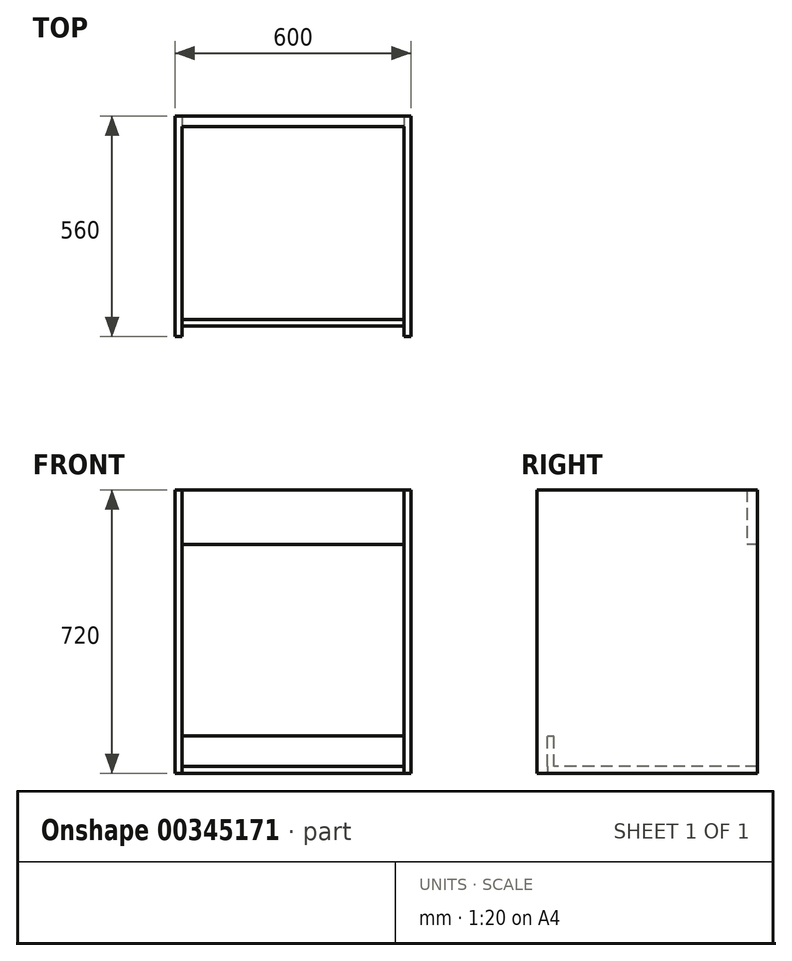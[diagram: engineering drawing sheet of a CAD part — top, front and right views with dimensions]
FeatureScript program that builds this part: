
annotation { "Feature Type Name" : "Feature", "Feature Type Description" : "" }
export const myFeature = defineFeature(function(context is Context, id is Id, definition is map)
    precondition{}
    {
        {
            var Q0;
            Q0=qCreatedBy(makeId("Front.planeOp"),FACE);
            var sketch = newSketch(context, id + "F0", { "sketchPlane" : qUnion([Q0])});
            skLineSegment(sketch, "E0.bottom", {"start": v(0, 0) * mm, "end": v(-52.5, 0) * mm});
            skLineSegment(sketch, "E0.top", {"start": v(0, 40.33) * mm, "end": v(-52.5, 40.33) * mm});
            skLineSegment(sketch, "E0.left", {"start": v(0, 0) * mm, "end": v(0, 40.33) * mm});
            skLineSegment(sketch, "E0.right", {"start": v(-52.5, 0) * mm, "end": v(-52.5, 40.33) * mm});
            skSolve(sketch);
        }
        {
            var Q0;
            Q0=makeQuery(id+"F0.imprint","IMPRINT",FACE,{"disambiguationData":[TD([[makeQuery(id+"F0.imprint","IMPRINT",EDGE,{"derivedFrom":sQuery(id+"F0.wireOp",EDGE,"E0.bottom")}),-1.0]])]});
            extrude(context, id + "F1", {"entities" : qUnion([Q0]), "oppositeDirection" : true, "depth" : 560 * mm});
        }
        {
            var Q0;
            Q0=makeQuery(id+"F1.opExtrude","SWEPT_FACE",FACE,{"disambiguationData":[OSD([sQuery(id+"F0.wireOp",EDGE,"E0.left")])]});
            extrude(context, id + "F2", {"entities" : qUnion([Q0]), "operationType" : NewBodyOperationType.ADD, "oppositeDirection" : true, "depth" : 600 * mm});
        }
        {
            var Q0;
            {var subQ0=sQuery(id+"F0.wireOp",EDGE,"E0.bottom");Q0=makeQuery(id+"F2.boolean.opBoolean","MERGE",FACE,{"derivedFrom":[makeQuery(id+"F1.opExtrude","SWEPT_FACE",FACE,{"disambiguationData":[OSD([subQ0])]}),makeQuery(id+"F2.opExtrude","SWEPT_FACE",FACE,{"disambiguationData":[OSD([subQ0,sQuery(id+"F0.wireOp",EDGE,"E0.left")])]})]});}
            extrude(context, id + "F3", {"entities" : qUnion([Q0]), "operationType" : NewBodyOperationType.ADD, "oppositeDirection" : true, "depth" : 720 * mm});
        }
        {
            var Q0;
            {var subQ0=sQuery(id+"F0.wireOp",EDGE,"E0.left");var subQ1=sQuery(id+"F0.wireOp",EDGE,"E0.bottom");Q0=makeQuery(id+"F3.boolean.opBoolean","MERGE",FACE,{"derivedFrom":[makeQuery(id+"F2.boolean.opBoolean","MERGE",FACE,{"derivedFrom":[makeQuery(id+"F1.opExtrude","CAP_FACE",FACE,{"disambiguationData":[OSD([subQ1,sQuery(id+"F0.wireOp",EDGE,"E0.top"),subQ0,sQuery(id+"F0.wireOp",EDGE,"E0.right")])],"isStart":false}),makeQuery(id+"F2.opExtrude","SWEPT_FACE",FACE,{"disambiguationData":[OSD([subQ0]),TDD([makeQuery(id+"F1.opExtrude","CAP_EDGE",EDGE,{"disambiguationData":[OSD([subQ0])],"isStart":false})])]})]}),makeQuery(id+"F3.opExtrude","SWEPT_FACE",FACE,{"disambiguationData":[OSD([subQ1,subQ0]),TDD([makeQuery(id+"F2.boolean.opBoolean","MERGE",EDGE,{"derivedFrom":[makeQuery(id+"F1.opExtrude","CAP_EDGE",EDGE,{"disambiguationData":[OSD([subQ1])],"isStart":false}),makeQuery(id+"F2.opExtrude","SWEPT_EDGE",EDGE,{"disambiguationData":[OSD([subQ1,subQ0]),TDD([makeQuery(id+"F1.opExtrude","CAP_VERTEX",VERTEX,{"disambiguationData":[OSD([subQ1,subQ0])],"isStart":false})])]})]})])]})]});}
            var Q1;
            Q1=makeQuery(id+"F3.opExtrude","CAP_FACE",FACE,{"disambiguationData":[OSD([sQuery(id+"F0.wireOp",EDGE,"E0.bottom"),sQuery(id+"F0.wireOp",EDGE,"E0.left")])],"isStart":false});
            var Q2;
            {var subQ0=sQuery(id+"F0.wireOp",EDGE,"E0.left");var subQ1=sQuery(id+"F0.wireOp",EDGE,"E0.bottom");Q2=makeQuery(id+"F3.boolean.opBoolean","MERGE",FACE,{"derivedFrom":[makeQuery(id+"F2.boolean.opBoolean","MERGE",FACE,{"derivedFrom":[makeQuery(id+"F1.opExtrude","CAP_FACE",FACE,{"disambiguationData":[OSD([subQ1,sQuery(id+"F0.wireOp",EDGE,"E0.top"),subQ0,sQuery(id+"F0.wireOp",EDGE,"E0.right")])],"isStart":true}),makeQuery(id+"F2.opExtrude","SWEPT_FACE",FACE,{"disambiguationData":[OSD([subQ0]),TDD([makeQuery(id+"F1.opExtrude","CAP_EDGE",EDGE,{"disambiguationData":[OSD([subQ0])],"isStart":true})])]})]}),makeQuery(id+"F3.opExtrude","SWEPT_FACE",FACE,{"disambiguationData":[OSD([subQ1,subQ0]),TDD([makeQuery(id+"F2.boolean.opBoolean","MERGE",EDGE,{"derivedFrom":[makeQuery(id+"F1.opExtrude","CAP_EDGE",EDGE,{"disambiguationData":[OSD([subQ1])],"isStart":true}),makeQuery(id+"F2.opExtrude","SWEPT_EDGE",EDGE,{"disambiguationData":[OSD([subQ1,subQ0]),TDD([makeQuery(id+"F1.opExtrude","CAP_VERTEX",VERTEX,{"disambiguationData":[OSD([subQ1,subQ0])],"isStart":true})])]})]})])]})]});}
            shell(context, id + "F4", {"entities" : qUnion([Q0, Q1, Q2]), "thickness" : 18 * mm});
        }
        {
            var Q0;
            {var subQ0=sQuery(id+"F0.wireOp",EDGE,"E0.left");var subQ1=sQuery(id+"F0.wireOp",EDGE,"E0.bottom");Q0=makeQuery(id+"F4.opShell","OFFSET_FACE",FACE,{"disambiguationData":[OSD([subQ1,subQ0]),TDD([makeQuery(id+"F3.boolean.opBoolean","MERGE",FACE,{"derivedFrom":[makeQuery(id+"F1.opExtrude","SWEPT_FACE",FACE,{"disambiguationData":[OSD([subQ0])]}),makeQuery(id+"F3.opExtrude","SWEPT_FACE",FACE,{"disambiguationData":[OSD([subQ1,subQ0]),TDD([makeQuery(id+"F1.opExtrude","SWEPT_EDGE",EDGE,{"disambiguationData":[OSD([subQ1,subQ0])]})])]})]})])]});}
            var sketch = newSketch(context, id + "F5", { "sketchPlane" : qUnion([Q0])});
            skLineSegment(sketch, "E1.bottom", {"start": v(-560, 720) * mm, "end": v(-532.8, 720) * mm});
            skLineSegment(sketch, "E1.top", {"start": v(-560, 581.74) * mm, "end": v(-532.8, 581.74) * mm});
            skLineSegment(sketch, "E1.left", {"start": v(-560, 720) * mm, "end": v(-560, 581.74) * mm});
            skLineSegment(sketch, "E1.right", {"start": v(-532.8, 720) * mm, "end": v(-532.8, 581.74) * mm});
            skSolve(sketch);
        }
        {
            var Q0;
            Q0=makeQuery(id+"F5.imprint","IMPRINT",FACE,{"disambiguationData":[TD([[makeQuery(id+"F5.imprint","IMPRINT",EDGE,{"derivedFrom":sQuery(id+"F5.wireOp",EDGE,"E1.bottom")}),-1.0]])]});
            extrude(context, id + "F6", {"entities" : qUnion([Q0]), "operationType" : NewBodyOperationType.ADD, "depth" : 562 * mm});
        }
        {
            var Q0;
            Q0=makeQuery(id+"F6.opExtrude","CAP_FACE",FACE,{"disambiguationData":[OSD([sQuery(id+"F5.wireOp",EDGE,"E1.bottom"),sQuery(id+"F5.wireOp",EDGE,"E1.top"),sQuery(id+"F5.wireOp",EDGE,"E1.left"),sQuery(id+"F5.wireOp",EDGE,"E1.right")])],"isStart":false});
            extrude(context, id + "F7", {"entities" : qUnion([Q0]), "operationType" : NewBodyOperationType.ADD, "depth" : 2 * mm});
        }
        {
            var Q0;
            {var subQ0=sQuery(id+"F0.wireOp",EDGE,"E0.left");var subQ1=sQuery(id+"F0.wireOp",EDGE,"E0.bottom");Q0=makeQuery(id+"F4.opShell","OFFSET_FACE",FACE,{"disambiguationData":[OSD([subQ1,subQ0]),TDD([makeQuery(id+"F3.boolean.opBoolean","MERGE",FACE,{"derivedFrom":[makeQuery(id+"F1.opExtrude","SWEPT_FACE",FACE,{"disambiguationData":[OSD([subQ0])]}),makeQuery(id+"F3.opExtrude","SWEPT_FACE",FACE,{"disambiguationData":[OSD([subQ1,subQ0]),TDD([makeQuery(id+"F1.opExtrude","SWEPT_EDGE",EDGE,{"disambiguationData":[OSD([subQ1,subQ0])]})])]})]})])]});}
            var sketch = newSketch(context, id + "F8", { "sketchPlane" : qUnion([Q0])});
            skLineSegment(sketch, "E2.bottom", {"start": v(-26.35, 18) * mm, "end": v(-43.1, 18) * mm});
            skLineSegment(sketch, "E2.top", {"start": v(-26.35, 95) * mm, "end": v(-43.1, 95) * mm});
            skLineSegment(sketch, "E2.left", {"start": v(-26.35, 18) * mm, "end": v(-26.35, 95) * mm});
            skLineSegment(sketch, "E2.right", {"start": v(-43.1, 18) * mm, "end": v(-43.1, 95) * mm});
            skSolve(sketch);
        }
        {
            var Q0;
            Q0=makeQuery(id+"F8.imprint","IMPRINT",FACE,{"disambiguationData":[TD([[makeQuery(id+"F8.imprint","IMPRINT",EDGE,{"derivedFrom":sQuery(id+"F8.wireOp",EDGE,"E2.bottom")}),1.0]])]});
            extrude(context, id + "F9", {"entities" : qUnion([Q0]), "operationType" : NewBodyOperationType.ADD, "depth" : 564 * mm});
        }
        {
            var Q0;
            {var subQ0=sQuery(id+"F0.wireOp",EDGE,"E0.left");var subQ1=sQuery(id+"F0.wireOp",EDGE,"E0.bottom");Q0=makeQuery(id+"F3.boolean.opBoolean","MERGE",FACE,{"derivedFrom":[makeQuery(id+"F2.boolean.opBoolean","MERGE",FACE,{"derivedFrom":[makeQuery(id+"F1.opExtrude","CAP_FACE",FACE,{"disambiguationData":[OSD([subQ1,sQuery(id+"F0.wireOp",EDGE,"E0.top"),subQ0,sQuery(id+"F0.wireOp",EDGE,"E0.right")])],"isStart":true}),makeQuery(id+"F2.opExtrude","SWEPT_FACE",FACE,{"disambiguationData":[OSD([subQ0]),TDD([makeQuery(id+"F1.opExtrude","CAP_EDGE",EDGE,{"disambiguationData":[OSD([subQ0])],"isStart":true})])]})]}),makeQuery(id+"F3.opExtrude","SWEPT_FACE",FACE,{"disambiguationData":[OSD([subQ1,subQ0]),TDD([makeQuery(id+"F2.boolean.opBoolean","MERGE",EDGE,{"derivedFrom":[makeQuery(id+"F1.opExtrude","CAP_EDGE",EDGE,{"disambiguationData":[OSD([subQ1])],"isStart":true}),makeQuery(id+"F2.opExtrude","SWEPT_EDGE",EDGE,{"disambiguationData":[OSD([subQ1,subQ0]),TDD([makeQuery(id+"F1.opExtrude","CAP_VERTEX",VERTEX,{"disambiguationData":[OSD([subQ1,subQ0])],"isStart":true})])]})]})])]})]});}
            var sketch = newSketch(context, id + "F10", { "sketchPlane" : qUnion([Q0])});
            skLineSegment(sketch, "E3", {"start": v(-18, 18) * mm, "end": v(-18, 0) * mm});
            skSolve(sketch);
        }
        {
            var Q0;
            {var subQ5=sQuery(id+"F10.wireOp",EDGE,"E3");Q0=makeQuery(id+"F10.imprint","IMPRINT",FACE,{"disambiguationData":[TD([[makeQuery(id+"F10.imprint","IMPRINT",EDGE,{"derivedFrom":subQ5}),-1.0]])]});}
            extrude(context, id + "F11", {"entities" : qUnion([Q0]), "operationType" : NewBodyOperationType.REMOVE, "oppositeDirection" : true, "depth" : 10 * mm});
        }
        {
            var Q0;
            Q0=makeQuery(id+"F11.boolean.opBoolean","COPY",FACE,{"derivedFrom":makeQuery(id+"F11.opExtrude","CAP_FACE",FACE,{"disambiguationData":[OSD([sQuery(id+"F0.wireOp",EDGE,"E0.bottom"),sQuery(id+"F0.wireOp",EDGE,"E0.left"),sQuery(id+"F10.wireOp",EDGE,"E3")])],"isStart":false})});
            var sketch = newSketch(context, id + "F12", { "sketchPlane" : qUnion([Q0])});
            skLineSegment(sketch, "E4", {"start": v(-582, 18) * mm, "end": v(-582, 0) * mm});
            skSolve(sketch);
        }
        {
            var Q0;
            {var subQ6=sQuery(id+"F12.wireOp",EDGE,"E4");Q0=makeQuery(id+"F12.imprint","IMPRINT",FACE,{"disambiguationData":[TD([[makeQuery(id+"F12.imprint","IMPRINT",EDGE,{"derivedFrom":subQ6}),-1.0]])]});}
            extrude(context, id + "F13", {"entities" : qUnion([Q0]), "operationType" : NewBodyOperationType.ADD, "depth" : 10 * mm});
        }
        {
            var Q0;
            Q0=makeQuery(id+"F11.boolean.opBoolean","COPY",FACE,{"derivedFrom":makeQuery(id+"F11.opExtrude","CAP_FACE",FACE,{"disambiguationData":[OSD([sQuery(id+"F0.wireOp",EDGE,"E0.bottom"),sQuery(id+"F0.wireOp",EDGE,"E0.left"),sQuery(id+"F10.wireOp",EDGE,"E3")])],"isStart":false})});
            extrude(context, id + "F14", {"entities" : qUnion([Q0]), "operationType" : NewBodyOperationType.REMOVE, "oppositeDirection" : true, "depth" : 16.5 * mm});
        }
    });
